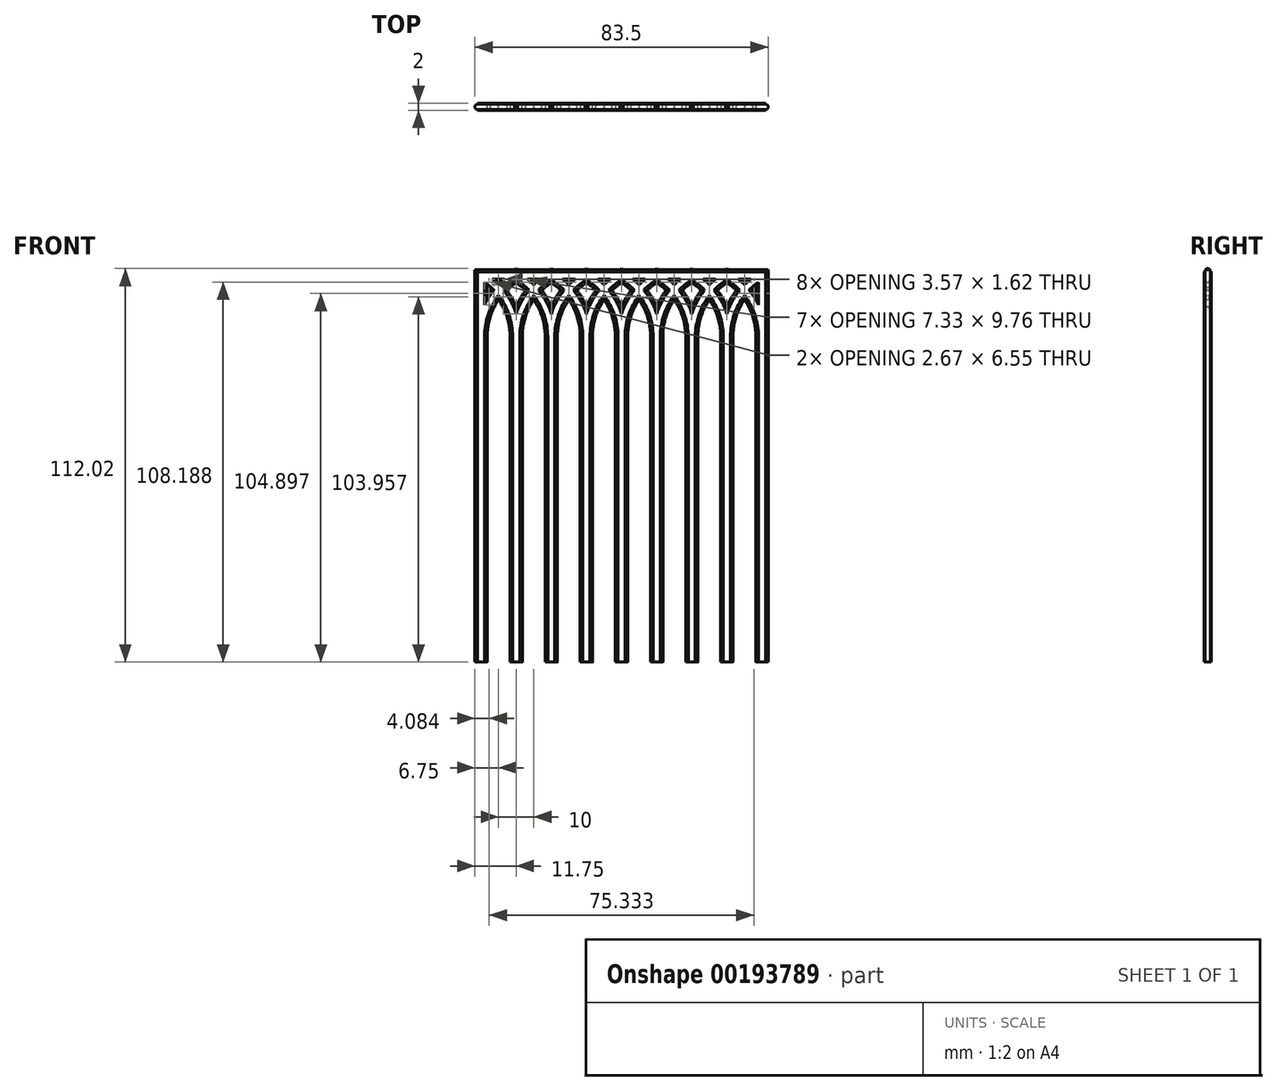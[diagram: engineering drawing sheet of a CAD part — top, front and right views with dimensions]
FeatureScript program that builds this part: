
annotation { "Feature Type Name" : "Feature", "Feature Type Description" : "" }
export const myFeature = defineFeature(function(context is Context, id is Id, definition is map)
    precondition{}
    {
        {
            var Q0;
            Q0=qCreatedBy(makeId("Front.planeOp"),FACE);
            var sketch = newSketch(context, id + "F0", { "sketchPlane" : qUnion([Q0])});
            skLineSegment(sketch, "E0", {"start": v(0, 0) * mm, "end": v(10, 0) * mm, "construction": true});
            skLineSegment(sketch, "E1", {"start": v(10, 0) * mm, "end": v(20, 0) * mm, "construction": true});
            skLineSegment(sketch, "E2", {"start": v(20, 0) * mm, "end": v(30, 0) * mm, "construction": true});
            skLineSegment(sketch, "E3", {"start": v(30, 0) * mm, "end": v(40, 0) * mm, "construction": true});
            skLineSegment(sketch, "E4", {"start": v(0, 0) * mm, "end": v(-10, 0) * mm, "construction": true});
            skLineSegment(sketch, "E5", {"start": v(-10, 0) * mm, "end": v(-20, 0) * mm, "construction": true});
            skLineSegment(sketch, "E6", {"start": v(-20, 0) * mm, "end": v(-30, 0) * mm, "construction": true});
            skLineSegment(sketch, "E7", {"start": v(-30, 0) * mm, "end": v(-40, 0) * mm, "construction": true});
            skLineSegment(sketch, "E8", {"start": v(-40, 0) * mm, "end": v(-40, 92.68) * mm});
            skLineSegment(sketch, "E9", {"start": v(-40, 110) * mm, "end": v(40, 110) * mm});
            skLineSegment(sketch, "E10", {"start": v(40, 110) * mm, "end": v(40, 92.68) * mm});
            skLineSegment(sketch, "E11", {"start": v(-20, 0) * mm, "end": v(-20, 110) * mm, "construction": true});
            skLineSegment(sketch, "E12", {"start": v(0, 0) * mm, "end": v(0, 110) * mm, "construction": true});
            skLineSegment(sketch, "E13", {"start": v(20, 0) * mm, "end": v(20, 110) * mm, "construction": true});
            skLineSegment(sketch, "E14", {"start": v(30, 0) * mm, "end": v(30, 110) * mm, "construction": true});
            skLineSegment(sketch, "E15", {"start": v(10, 0) * mm, "end": v(10, 110) * mm, "construction": true});
            skLineSegment(sketch, "E16", {"start": v(-10, 0) * mm, "end": v(-10, 110) * mm, "construction": true});
            skLineSegment(sketch, "E17", {"start": v(-30, 0) * mm, "end": v(-30, 110) * mm, "construction": true});
            skCircle(sketch, "E18", {"center": v(-30, 110) * mm, "radius": 20 * mm, "construction": true});
            skLineSegment(sketch, "E19", {"start": v(-40, 92.68) * mm, "end": v(-30, 92.68) * mm, "construction": true});
            skLineSegment(sketch, "E20", {"start": v(-30, 92.68) * mm, "end": v(-20, 92.68) * mm, "construction": true});
            skLineSegment(sketch, "E21", {"start": v(-20, 92.68) * mm, "end": v(-10, 92.68) * mm, "construction": true});
            skLineSegment(sketch, "E22", {"start": v(0, 92.68) * mm, "end": v(-10, 92.68) * mm, "construction": true});
            skLineSegment(sketch, "E23", {"start": v(0, 92.68) * mm, "end": v(10, 92.68) * mm, "construction": true});
            skLineSegment(sketch, "E24", {"start": v(10, 92.68) * mm, "end": v(20, 92.68) * mm, "construction": true});
            skLineSegment(sketch, "E25", {"start": v(30, 92.68) * mm, "end": v(20, 92.68) * mm, "construction": true});
            skLineSegment(sketch, "E26", {"start": v(30, 92.68) * mm, "end": v(40, 92.68) * mm, "construction": true});
            skArc(sketch, "E27", {"start": v(-40, 92.68) * mm, "mid": v(-37.32, 102.68) * mm, "end": v(-30, 110) * mm});
            skArc(sketch, "E28", {"start": v(-20, 110) * mm, "mid": v(-27.32, 102.68) * mm, "end": v(-30, 92.68) * mm});
            skArc(sketch, "E29", {"start": v(-10, 110) * mm, "mid": v(-17.32, 102.68) * mm, "end": v(-20, 92.68) * mm});
            skArc(sketch, "E30", {"start": v(-10, 92.68) * mm, "mid": v(-7.32, 102.68) * mm, "end": v(0, 110) * mm});
            skArc(sketch, "E31", {"start": v(10, 110) * mm, "mid": v(2.68, 102.68) * mm, "end": v(0, 92.68) * mm});
            skArc(sketch, "E32", {"start": v(20, 110) * mm, "mid": v(12.68, 102.68) * mm, "end": v(10, 92.68) * mm});
            skArc(sketch, "E33", {"start": v(20, 92.68) * mm, "mid": v(22.68, 102.68) * mm, "end": v(30, 110) * mm});
            skLineSegment(sketch, "E34", {"start": v(40, 92.68) * mm, "end": v(50, 92.68) * mm, "construction": true});
            skLineSegment(sketch, "E35", {"start": v(-40, 92.68) * mm, "end": v(-50, 92.68) * mm, "construction": true});
            skArc(sketch, "E36", {"start": v(-40, 110) * mm, "mid": v(-32.68, 102.68) * mm, "end": v(-30, 92.68) * mm});
            skArc(sketch, "E37", {"start": v(-20, 110) * mm, "mid": v(-12.68, 102.68) * mm, "end": v(-10, 92.68) * mm});
            skArc(sketch, "E38", {"start": v(-30, 110) * mm, "mid": v(-22.68, 102.68) * mm, "end": v(-20, 92.68) * mm});
            skArc(sketch, "E39", {"start": v(0, 110) * mm, "mid": v(7.32, 102.68) * mm, "end": v(10, 92.68) * mm});
            skArc(sketch, "E40", {"start": v(10, 110) * mm, "mid": v(17.32, 102.68) * mm, "end": v(20, 92.68) * mm});
            skArc(sketch, "E41", {"start": v(20, 110) * mm, "mid": v(27.32, 102.68) * mm, "end": v(30, 92.68) * mm});
            skArc(sketch, "E42", {"start": v(30, 110) * mm, "mid": v(37.32, 102.68) * mm, "end": v(40, 92.68) * mm});
            skArc(sketch, "E43", {"start": v(30, 92.68) * mm, "mid": v(32.68, 102.68) * mm, "end": v(40, 110) * mm});
            skArc(sketch, "E44", {"start": v(-10, 110) * mm, "mid": v(-2.68, 102.68) * mm, "end": v(0, 92.68) * mm});
            skLineSegment(sketch, "E45", {"start": v(-30, 92.68) * mm, "end": v(-30, 0) * mm});
            skLineSegment(sketch, "E46", {"start": v(-20, 92.68) * mm, "end": v(-20, 0) * mm});
            skLineSegment(sketch, "E47", {"start": v(-10, 0) * mm, "end": v(-10, 92.68) * mm});
            skLineSegment(sketch, "E48", {"start": v(0, 92.68) * mm, "end": v(0, 0) * mm});
            skLineSegment(sketch, "E49", {"start": v(10, 92.68) * mm, "end": v(10, 0) * mm});
            skLineSegment(sketch, "E50", {"start": v(20, 0) * mm, "end": v(20, 92.68) * mm});
            skLineSegment(sketch, "E51", {"start": v(30, 92.68) * mm, "end": v(30, 0) * mm});
            skLineSegment(sketch, "E52", {"start": v(-40, 92.68) * mm, "end": v(-40, 110) * mm});
            skLineSegment(sketch, "E53", {"start": v(40, 92.68) * mm, "end": v(40, 0) * mm});
            skSolve(sketch);
        }
        {
            var Q0;
            Q0=qCreatedBy(makeId("Top.planeOp"),FACE);
            var sketch = newSketch(context, id + "F1", { "sketchPlane" : qUnion([Q0])});
            skPoint(sketch, "E54.0", {"position": v(-40, 0) * mm});
            skLineSegment(sketch, "E55.bottom", {"start": v(-39, 1) * mm, "end": v(-41, 1) * mm});
            skLineSegment(sketch, "E55.top", {"start": v(-39, -1) * mm, "end": v(-41, -1) * mm});
            skLineSegment(sketch, "E55.left", {"start": v(-39, 1) * mm, "end": v(-39, -1) * mm});
            skLineSegment(sketch, "E55.right", {"start": v(-41, 1) * mm, "end": v(-41, -1) * mm});
            skCircle(sketch, "E56", {"center": v(-39, 0) * mm, "radius": 0.75 * mm});
            skCircle(sketch, "E57", {"center": v(-41, 0) * mm, "radius": 0.75 * mm});
            skPoint(sketch, "E58.1.0.0", {"position": v(-30, 0) * mm});
            skCircle(sketch, "E58.1.0.1", {"center": v(-31, 0) * mm, "radius": 0.75 * mm});
            skLineSegment(sketch, "E58.1.0.2", {"start": v(-29, -1) * mm, "end": v(-31, -1) * mm});
            skLineSegment(sketch, "E58.1.0.3", {"start": v(-31, 1) * mm, "end": v(-31, -1) * mm});
            skLineSegment(sketch, "E58.1.0.4", {"start": v(-29, 1) * mm, "end": v(-31, 1) * mm});
            skCircle(sketch, "E58.1.0.5", {"center": v(-29, 0) * mm, "radius": 0.75 * mm});
            skLineSegment(sketch, "E58.1.0.6", {"start": v(-29, 1) * mm, "end": v(-29, -1) * mm});
            skPoint(sketch, "E58.2.0.0", {"position": v(-20, 0) * mm});
            skCircle(sketch, "E58.2.0.1", {"center": v(-21, 0) * mm, "radius": 0.75 * mm});
            skLineSegment(sketch, "E58.2.0.2", {"start": v(-19, -1) * mm, "end": v(-21, -1) * mm});
            skLineSegment(sketch, "E58.2.0.3", {"start": v(-21, 1) * mm, "end": v(-21, -1) * mm});
            skLineSegment(sketch, "E58.2.0.4", {"start": v(-19, 1) * mm, "end": v(-21, 1) * mm});
            skCircle(sketch, "E58.2.0.5", {"center": v(-19, 0) * mm, "radius": 0.75 * mm});
            skLineSegment(sketch, "E58.2.0.6", {"start": v(-19, 1) * mm, "end": v(-19, -1) * mm});
            skPoint(sketch, "E58.3.0.0", {"position": v(-10, 0) * mm});
            skCircle(sketch, "E58.3.0.1", {"center": v(-11, 0) * mm, "radius": 0.75 * mm});
            skLineSegment(sketch, "E58.3.0.2", {"start": v(-9, -1) * mm, "end": v(-11, -1) * mm});
            skLineSegment(sketch, "E58.3.0.3", {"start": v(-11, 1) * mm, "end": v(-11, -1) * mm});
            skLineSegment(sketch, "E58.3.0.4", {"start": v(-9, 1) * mm, "end": v(-11, 1) * mm});
            skCircle(sketch, "E58.3.0.5", {"center": v(-9, 0) * mm, "radius": 0.75 * mm});
            skLineSegment(sketch, "E58.3.0.6", {"start": v(-9, 1) * mm, "end": v(-9, -1) * mm});
            skPoint(sketch, "E58.4.0.0", {"position": v(0, 0) * mm});
            skCircle(sketch, "E58.4.0.1", {"center": v(-1, 0) * mm, "radius": 0.75 * mm});
            skLineSegment(sketch, "E58.4.0.2", {"start": v(1, -1) * mm, "end": v(-1, -1) * mm});
            skLineSegment(sketch, "E58.4.0.3", {"start": v(-1, 1) * mm, "end": v(-1, -1) * mm});
            skLineSegment(sketch, "E58.4.0.4", {"start": v(1, 1) * mm, "end": v(-1, 1) * mm});
            skCircle(sketch, "E58.4.0.5", {"center": v(1, 0) * mm, "radius": 0.75 * mm});
            skLineSegment(sketch, "E58.4.0.6", {"start": v(1, 1) * mm, "end": v(1, -1) * mm});
            skPoint(sketch, "E58.5.0.0", {"position": v(10, 0) * mm});
            skCircle(sketch, "E58.5.0.1", {"center": v(9, 0) * mm, "radius": 0.75 * mm});
            skLineSegment(sketch, "E58.5.0.2", {"start": v(11, -1) * mm, "end": v(9, -1) * mm});
            skLineSegment(sketch, "E58.5.0.3", {"start": v(9, 1) * mm, "end": v(9, -1) * mm});
            skLineSegment(sketch, "E58.5.0.4", {"start": v(11, 1) * mm, "end": v(9, 1) * mm});
            skCircle(sketch, "E58.5.0.5", {"center": v(11, 0) * mm, "radius": 0.75 * mm});
            skLineSegment(sketch, "E58.5.0.6", {"start": v(11, 1) * mm, "end": v(11, -1) * mm});
            skPoint(sketch, "E58.6.0.0", {"position": v(20, 0) * mm});
            skCircle(sketch, "E58.6.0.1", {"center": v(19, 0) * mm, "radius": 0.75 * mm});
            skLineSegment(sketch, "E58.6.0.2", {"start": v(21, -1) * mm, "end": v(19, -1) * mm});
            skLineSegment(sketch, "E58.6.0.3", {"start": v(19, 1) * mm, "end": v(19, -1) * mm});
            skLineSegment(sketch, "E58.6.0.4", {"start": v(21, 1) * mm, "end": v(19, 1) * mm});
            skCircle(sketch, "E58.6.0.5", {"center": v(21, 0) * mm, "radius": 0.75 * mm});
            skLineSegment(sketch, "E58.6.0.6", {"start": v(21, 1) * mm, "end": v(21, -1) * mm});
            skPoint(sketch, "E58.7.0.0", {"position": v(30, 0) * mm});
            skCircle(sketch, "E58.7.0.1", {"center": v(29, 0) * mm, "radius": 0.75 * mm});
            skLineSegment(sketch, "E58.7.0.2", {"start": v(31, -1) * mm, "end": v(29, -1) * mm});
            skLineSegment(sketch, "E58.7.0.3", {"start": v(29, 1) * mm, "end": v(29, -1) * mm});
            skLineSegment(sketch, "E58.7.0.4", {"start": v(31, 1) * mm, "end": v(29, 1) * mm});
            skCircle(sketch, "E58.7.0.5", {"center": v(31, 0) * mm, "radius": 0.75 * mm});
            skLineSegment(sketch, "E58.7.0.6", {"start": v(31, 1) * mm, "end": v(31, -1) * mm});
            skPoint(sketch, "E58.8.0.0", {"position": v(40, 0) * mm});
            skCircle(sketch, "E58.8.0.1", {"center": v(39, 0) * mm, "radius": 0.75 * mm});
            skLineSegment(sketch, "E58.8.0.2", {"start": v(41, -1) * mm, "end": v(39, -1) * mm});
            skLineSegment(sketch, "E58.8.0.3", {"start": v(39, 1) * mm, "end": v(39, -1) * mm});
            skLineSegment(sketch, "E58.8.0.4", {"start": v(41, 1) * mm, "end": v(39, 1) * mm});
            skCircle(sketch, "E58.8.0.5", {"center": v(41, 0) * mm, "radius": 0.75 * mm});
            skLineSegment(sketch, "E58.8.0.6", {"start": v(41, 1) * mm, "end": v(41, -1) * mm});
            skLineSegment(sketch, "E58.direction1", {"start": v(-40, 0) * mm, "end": v(-30, 0) * mm, "construction": true});
            skSolve(sketch);
        }
        {
            var Q0;
            {var subQ0=sQuery(id+"F1.wireOp",EDGE,"E57");var subQ1=sQuery(id+"F1.wireOp",EDGE,"E55.right");var subQ2=makeQuery(id+"F1.imprint","INTERSECT",VERTEX,{"disambiguationData":[OD(0.0)],"derivedFrom":[subQ1,subQ0]});Q0=makeQuery(id+"F1.imprint","IMPRINT",FACE,{"disambiguationData":[TD([[makeQuery(id+"F1.imprint","IMPRINT",EDGE,{"disambiguationData":[TD([[subQ2,-1.0]])],"derivedFrom":subQ1}),-1.0]])]});}
            var Q1;
            {var subQ0=sQuery(id+"F1.wireOp",EDGE,"E57");var subQ1=sQuery(id+"F1.wireOp",EDGE,"E55.right");var subQ2=makeQuery(id+"F1.imprint","INTERSECT",VERTEX,{"disambiguationData":[OD(0.0)],"derivedFrom":[subQ1,subQ0]});Q1=makeQuery(id+"F1.imprint","IMPRINT",FACE,{"disambiguationData":[TD([[makeQuery(id+"F1.imprint","IMPRINT",EDGE,{"disambiguationData":[TD([[subQ2,-1.0]])],"derivedFrom":subQ1}),1.0]])]});}
            var Q2;
            {var subQ4=sQuery(id+"F1.wireOp",EDGE,"E55.bottom");Q2=makeQuery(id+"F1.imprint","IMPRINT",FACE,{"disambiguationData":[TD([[makeQuery(id+"F1.imprint","IMPRINT",EDGE,{"derivedFrom":subQ4}),1.0]])]});}
            var Q3;
            {var subQ0=sQuery(id+"F1.wireOp",EDGE,"E56");var subQ1=sQuery(id+"F1.wireOp",EDGE,"E55.left");var subQ2=makeQuery(id+"F1.imprint","INTERSECT",VERTEX,{"disambiguationData":[OD(0.0)],"derivedFrom":[subQ1,subQ0]});Q3=makeQuery(id+"F1.imprint","IMPRINT",FACE,{"disambiguationData":[TD([[makeQuery(id+"F1.imprint","IMPRINT",EDGE,{"disambiguationData":[TD([[subQ2,-1.0]])],"derivedFrom":subQ1}),-1.0]])]});}
            var Q4;
            {var subQ0=sQuery(id+"F1.wireOp",EDGE,"E56");var subQ1=sQuery(id+"F1.wireOp",EDGE,"E55.left");var subQ2=makeQuery(id+"F1.imprint","INTERSECT",VERTEX,{"disambiguationData":[OD(0.0)],"derivedFrom":[subQ1,subQ0]});Q4=makeQuery(id+"F1.imprint","IMPRINT",FACE,{"disambiguationData":[TD([[makeQuery(id+"F1.imprint","IMPRINT",EDGE,{"disambiguationData":[TD([[subQ2,-1.0]])],"derivedFrom":subQ1}),1.0]])]});}
            var Q5;
            Q5=sQuery(id+"F0.wireOp",EDGE,"E8");
            var Q6;
            Q6=sQuery(id+"F0.wireOp",EDGE,"E9");
            var Q7;
            Q7=sQuery(id+"F0.wireOp",EDGE,"E52");
            var Q8;
            Q8=sQuery(id+"F0.wireOp",EDGE,"E10");
            sweep(context, id + "F2", {"profiles" : qUnion([Q0, Q1, Q2, Q3, Q4]), "path" : qUnion([Q5, Q6, Q7, Q8])});
        }
        {
            var Q0;
            Q0=makeQuery(id+"F2.opSweep","CAP_FACE",FACE,{"disambiguationData":[OSD([sQuery(id+"F0.wireOp",VERTEX,"E8.start"),sQuery(id+"F1.wireOp",EDGE,"E55.bottom"),sQuery(id+"F1.wireOp",EDGE,"E55.top"),sQuery(id+"F1.wireOp",EDGE,"E55.left"),sQuery(id+"F1.wireOp",EDGE,"E55.right"),sQuery(id+"F1.wireOp",EDGE,"E56"),sQuery(id+"F1.wireOp",EDGE,"E57")])],"isStart":true});
            var Q1;
            Q1=sQuery(id+"F0.wireOp",EDGE,"E27");
            var Q2;
            Q2=sQuery(id+"F0.wireOp",EDGE,"E8");
            var Q3;
            Q3=sQuery(id+"F0.wireOp",EDGE,"E38");
            sweep(context, id + "F3", {"operationType" : NewBodyOperationType.ADD, "profiles" : qUnion([Q0]), "path" : qUnion([Q1, Q2, Q3])});
        }
        {
            var Q0;
            {var subQ1=sQuery(id+"F1.wireOp",EDGE,"E58.1.0.2");Q0=makeQuery(id+"F1.imprint","IMPRINT",FACE,{"disambiguationData":[TD([[makeQuery(id+"F1.imprint","IMPRINT",EDGE,{"derivedFrom":subQ1}),-1.0]])]});}
            var Q1;
            {var subQ0=sQuery(id+"F1.wireOp",EDGE,"E58.1.0.3");var subQ1=sQuery(id+"F1.wireOp",EDGE,"E58.1.0.1");var subQ2=makeQuery(id+"F1.imprint","INTERSECT",VERTEX,{"disambiguationData":[OD(0.0)],"derivedFrom":[subQ1,subQ0]});Q1=makeQuery(id+"F1.imprint","IMPRINT",FACE,{"disambiguationData":[TD([[makeQuery(id+"F1.imprint","IMPRINT",EDGE,{"disambiguationData":[TD([[subQ2,1.0]])],"derivedFrom":subQ1}),1.0]])]});}
            var Q2;
            {var subQ0=sQuery(id+"F1.wireOp",EDGE,"E58.1.0.3");var subQ1=sQuery(id+"F1.wireOp",EDGE,"E58.1.0.1");var subQ2=makeQuery(id+"F1.imprint","INTERSECT",VERTEX,{"disambiguationData":[OD(0.0)],"derivedFrom":[subQ1,subQ0]});Q2=makeQuery(id+"F1.imprint","IMPRINT",FACE,{"disambiguationData":[TD([[makeQuery(id+"F1.imprint","IMPRINT",EDGE,{"disambiguationData":[TD([[subQ2,-1.0]])],"derivedFrom":subQ1}),1.0]])]});}
            var Q3;
            {var subQ0=sQuery(id+"F1.wireOp",EDGE,"E58.1.0.6");var subQ1=sQuery(id+"F1.wireOp",EDGE,"E58.1.0.5");var subQ2=makeQuery(id+"F1.imprint","INTERSECT",VERTEX,{"disambiguationData":[OD(0.0)],"derivedFrom":[subQ1,subQ0]});Q3=makeQuery(id+"F1.imprint","IMPRINT",FACE,{"disambiguationData":[TD([[makeQuery(id+"F1.imprint","IMPRINT",EDGE,{"disambiguationData":[TD([[subQ2,-1.0]])],"derivedFrom":subQ1}),1.0]])]});}
            var Q4;
            {var subQ0=sQuery(id+"F1.wireOp",EDGE,"E58.1.0.6");var subQ1=sQuery(id+"F1.wireOp",EDGE,"E58.1.0.5");var subQ2=makeQuery(id+"F1.imprint","INTERSECT",VERTEX,{"disambiguationData":[OD(0.0)],"derivedFrom":[subQ1,subQ0]});Q4=makeQuery(id+"F1.imprint","IMPRINT",FACE,{"disambiguationData":[TD([[makeQuery(id+"F1.imprint","IMPRINT",EDGE,{"disambiguationData":[TD([[subQ2,1.0]])],"derivedFrom":subQ1}),1.0]])]});}
            var Q5;
            Q5=sQuery(id+"F0.wireOp",EDGE,"E45");
            var Q6;
            Q6=sQuery(id+"F0.wireOp",EDGE,"E28");
            var Q7;
            Q7=sQuery(id+"F0.wireOp",EDGE,"E37");
            sweep(context, id + "F4", {"operationType" : NewBodyOperationType.ADD, "profiles" : qUnion([Q0, Q1, Q2, Q3, Q4]), "path" : qUnion([Q5, Q6, Q7])});
        }
        {
            var Q0;
            {var subQ1=sQuery(id+"F1.wireOp",EDGE,"E58.2.0.2");Q0=makeQuery(id+"F1.imprint","IMPRINT",FACE,{"disambiguationData":[TD([[makeQuery(id+"F1.imprint","IMPRINT",EDGE,{"derivedFrom":subQ1}),-1.0]])]});}
            var Q1;
            {var subQ0=sQuery(id+"F1.wireOp",EDGE,"E58.2.0.6");var subQ1=sQuery(id+"F1.wireOp",EDGE,"E58.2.0.5");var subQ2=makeQuery(id+"F1.imprint","INTERSECT",VERTEX,{"disambiguationData":[OD(0.0)],"derivedFrom":[subQ1,subQ0]});Q1=makeQuery(id+"F1.imprint","IMPRINT",FACE,{"disambiguationData":[TD([[makeQuery(id+"F1.imprint","IMPRINT",EDGE,{"disambiguationData":[TD([[subQ2,-1.0]])],"derivedFrom":subQ1}),1.0]])]});}
            var Q2;
            {var subQ0=sQuery(id+"F1.wireOp",EDGE,"E58.2.0.6");var subQ1=sQuery(id+"F1.wireOp",EDGE,"E58.2.0.5");var subQ2=makeQuery(id+"F1.imprint","INTERSECT",VERTEX,{"disambiguationData":[OD(0.0)],"derivedFrom":[subQ1,subQ0]});Q2=makeQuery(id+"F1.imprint","IMPRINT",FACE,{"disambiguationData":[TD([[makeQuery(id+"F1.imprint","IMPRINT",EDGE,{"disambiguationData":[TD([[subQ2,1.0]])],"derivedFrom":subQ1}),1.0]])]});}
            var Q3;
            {var subQ0=sQuery(id+"F1.wireOp",EDGE,"E58.2.0.3");var subQ1=sQuery(id+"F1.wireOp",EDGE,"E58.2.0.1");var subQ2=makeQuery(id+"F1.imprint","INTERSECT",VERTEX,{"disambiguationData":[OD(0.0)],"derivedFrom":[subQ1,subQ0]});Q3=makeQuery(id+"F1.imprint","IMPRINT",FACE,{"disambiguationData":[TD([[makeQuery(id+"F1.imprint","IMPRINT",EDGE,{"disambiguationData":[TD([[subQ2,-1.0]])],"derivedFrom":subQ1}),1.0]])]});}
            var Q4;
            {var subQ0=sQuery(id+"F1.wireOp",EDGE,"E58.2.0.3");var subQ1=sQuery(id+"F1.wireOp",EDGE,"E58.2.0.1");var subQ2=makeQuery(id+"F1.imprint","INTERSECT",VERTEX,{"disambiguationData":[OD(0.0)],"derivedFrom":[subQ1,subQ0]});Q4=makeQuery(id+"F1.imprint","IMPRINT",FACE,{"disambiguationData":[TD([[makeQuery(id+"F1.imprint","IMPRINT",EDGE,{"disambiguationData":[TD([[subQ2,1.0]])],"derivedFrom":subQ1}),1.0]])]});}
            var Q5;
            Q5=sQuery(id+"F0.wireOp",EDGE,"E46");
            var Q6;
            Q6=sQuery(id+"F0.wireOp",EDGE,"E29");
            var Q7;
            Q7=sQuery(id+"F0.wireOp",EDGE,"E44");
            sweep(context, id + "F5", {"operationType" : NewBodyOperationType.ADD, "profiles" : qUnion([Q0, Q1, Q2, Q3, Q4]), "path" : qUnion([Q5, Q6, Q7])});
        }
        {
            var Q0;
            {var subQ0=sQuery(id+"F1.wireOp",EDGE,"E58.3.0.3");var subQ1=sQuery(id+"F1.wireOp",EDGE,"E58.3.0.1");var subQ2=makeQuery(id+"F1.imprint","INTERSECT",VERTEX,{"disambiguationData":[OD(0.0)],"derivedFrom":[subQ1,subQ0]});Q0=makeQuery(id+"F1.imprint","IMPRINT",FACE,{"disambiguationData":[TD([[makeQuery(id+"F1.imprint","IMPRINT",EDGE,{"disambiguationData":[TD([[subQ2,1.0]])],"derivedFrom":subQ1}),1.0]])]});}
            var Q1;
            {var subQ0=sQuery(id+"F1.wireOp",EDGE,"E58.3.0.3");var subQ1=sQuery(id+"F1.wireOp",EDGE,"E58.3.0.1");var subQ2=makeQuery(id+"F1.imprint","INTERSECT",VERTEX,{"disambiguationData":[OD(0.0)],"derivedFrom":[subQ1,subQ0]});Q1=makeQuery(id+"F1.imprint","IMPRINT",FACE,{"disambiguationData":[TD([[makeQuery(id+"F1.imprint","IMPRINT",EDGE,{"disambiguationData":[TD([[subQ2,-1.0]])],"derivedFrom":subQ1}),1.0]])]});}
            var Q2;
            {var subQ0=sQuery(id+"F1.wireOp",EDGE,"E58.3.0.6");var subQ1=sQuery(id+"F1.wireOp",EDGE,"E58.3.0.5");var subQ2=makeQuery(id+"F1.imprint","INTERSECT",VERTEX,{"disambiguationData":[OD(0.0)],"derivedFrom":[subQ1,subQ0]});Q2=makeQuery(id+"F1.imprint","IMPRINT",FACE,{"disambiguationData":[TD([[makeQuery(id+"F1.imprint","IMPRINT",EDGE,{"disambiguationData":[TD([[subQ2,1.0]])],"derivedFrom":subQ1}),1.0]])]});}
            var Q3;
            {var subQ1=sQuery(id+"F1.wireOp",EDGE,"E58.3.0.2");Q3=makeQuery(id+"F1.imprint","IMPRINT",FACE,{"disambiguationData":[TD([[makeQuery(id+"F1.imprint","IMPRINT",EDGE,{"derivedFrom":subQ1}),-1.0]])]});}
            var Q4;
            {var subQ0=sQuery(id+"F1.wireOp",EDGE,"E58.3.0.6");var subQ1=sQuery(id+"F1.wireOp",EDGE,"E58.3.0.5");var subQ2=makeQuery(id+"F1.imprint","INTERSECT",VERTEX,{"disambiguationData":[OD(0.0)],"derivedFrom":[subQ1,subQ0]});Q4=makeQuery(id+"F1.imprint","IMPRINT",FACE,{"disambiguationData":[TD([[makeQuery(id+"F1.imprint","IMPRINT",EDGE,{"disambiguationData":[TD([[subQ2,-1.0]])],"derivedFrom":subQ1}),1.0]])]});}
            var Q5;
            Q5=sQuery(id+"F0.wireOp",EDGE,"E47");
            var Q6;
            Q6=sQuery(id+"F0.wireOp",EDGE,"E30");
            var Q7;
            Q7=sQuery(id+"F0.wireOp",EDGE,"E39");
            sweep(context, id + "F6", {"operationType" : NewBodyOperationType.ADD, "profiles" : qUnion([Q0, Q1, Q2, Q3, Q4]), "path" : qUnion([Q5, Q6, Q7])});
        }
        {
            var Q0;
            {var subQ0=sQuery(id+"F1.wireOp",EDGE,"E58.4.0.6");var subQ1=sQuery(id+"F1.wireOp",EDGE,"E58.4.0.5");var subQ2=makeQuery(id+"F1.imprint","INTERSECT",VERTEX,{"disambiguationData":[OD(0.0)],"derivedFrom":[subQ1,subQ0]});Q0=makeQuery(id+"F1.imprint","IMPRINT",FACE,{"disambiguationData":[TD([[makeQuery(id+"F1.imprint","IMPRINT",EDGE,{"disambiguationData":[TD([[subQ2,-1.0]])],"derivedFrom":subQ1}),1.0]])]});}
            var Q1;
            {var subQ1=sQuery(id+"F1.wireOp",EDGE,"E58.4.0.2");Q1=makeQuery(id+"F1.imprint","IMPRINT",FACE,{"disambiguationData":[TD([[makeQuery(id+"F1.imprint","IMPRINT",EDGE,{"derivedFrom":subQ1}),-1.0]])]});}
            var Q2;
            {var subQ0=sQuery(id+"F1.wireOp",EDGE,"E58.4.0.3");var subQ1=sQuery(id+"F1.wireOp",EDGE,"E58.4.0.1");var subQ2=makeQuery(id+"F1.imprint","INTERSECT",VERTEX,{"disambiguationData":[OD(0.0)],"derivedFrom":[subQ1,subQ0]});Q2=makeQuery(id+"F1.imprint","IMPRINT",FACE,{"disambiguationData":[TD([[makeQuery(id+"F1.imprint","IMPRINT",EDGE,{"disambiguationData":[TD([[subQ2,-1.0]])],"derivedFrom":subQ1}),1.0]])]});}
            var Q3;
            {var subQ0=sQuery(id+"F1.wireOp",EDGE,"E58.4.0.6");var subQ1=sQuery(id+"F1.wireOp",EDGE,"E58.4.0.5");var subQ2=makeQuery(id+"F1.imprint","INTERSECT",VERTEX,{"disambiguationData":[OD(0.0)],"derivedFrom":[subQ1,subQ0]});Q3=makeQuery(id+"F1.imprint","IMPRINT",FACE,{"disambiguationData":[TD([[makeQuery(id+"F1.imprint","IMPRINT",EDGE,{"disambiguationData":[TD([[subQ2,1.0]])],"derivedFrom":subQ1}),1.0]])]});}
            var Q4;
            {var subQ0=sQuery(id+"F1.wireOp",EDGE,"E58.4.0.3");var subQ1=sQuery(id+"F1.wireOp",EDGE,"E58.4.0.1");var subQ2=makeQuery(id+"F1.imprint","INTERSECT",VERTEX,{"disambiguationData":[OD(0.0)],"derivedFrom":[subQ1,subQ0]});Q4=makeQuery(id+"F1.imprint","IMPRINT",FACE,{"disambiguationData":[TD([[makeQuery(id+"F1.imprint","IMPRINT",EDGE,{"disambiguationData":[TD([[subQ2,1.0]])],"derivedFrom":subQ1}),1.0]])]});}
            var Q5;
            Q5=sQuery(id+"F0.wireOp",EDGE,"E48");
            var Q6;
            Q6=sQuery(id+"F0.wireOp",EDGE,"E31");
            var Q7;
            Q7=sQuery(id+"F0.wireOp",EDGE,"E40");
            sweep(context, id + "F7", {"operationType" : NewBodyOperationType.ADD, "profiles" : qUnion([Q0, Q1, Q2, Q3, Q4]), "path" : qUnion([Q5, Q6, Q7])});
        }
        {
            var Q0;
            {var subQ0=sQuery(id+"F1.wireOp",EDGE,"E58.5.0.3");var subQ1=sQuery(id+"F1.wireOp",EDGE,"E58.5.0.1");var subQ2=makeQuery(id+"F1.imprint","INTERSECT",VERTEX,{"disambiguationData":[OD(0.0)],"derivedFrom":[subQ1,subQ0]});Q0=makeQuery(id+"F1.imprint","IMPRINT",FACE,{"disambiguationData":[TD([[makeQuery(id+"F1.imprint","IMPRINT",EDGE,{"disambiguationData":[TD([[subQ2,-1.0]])],"derivedFrom":subQ1}),1.0]])]});}
            var Q1;
            {var subQ0=sQuery(id+"F1.wireOp",EDGE,"E58.5.0.6");var subQ1=sQuery(id+"F1.wireOp",EDGE,"E58.5.0.5");var subQ2=makeQuery(id+"F1.imprint","INTERSECT",VERTEX,{"disambiguationData":[OD(0.0)],"derivedFrom":[subQ1,subQ0]});Q1=makeQuery(id+"F1.imprint","IMPRINT",FACE,{"disambiguationData":[TD([[makeQuery(id+"F1.imprint","IMPRINT",EDGE,{"disambiguationData":[TD([[subQ2,1.0]])],"derivedFrom":subQ1}),1.0]])]});}
            var Q2;
            {var subQ0=sQuery(id+"F1.wireOp",EDGE,"E58.5.0.3");var subQ1=sQuery(id+"F1.wireOp",EDGE,"E58.5.0.1");var subQ2=makeQuery(id+"F1.imprint","INTERSECT",VERTEX,{"disambiguationData":[OD(0.0)],"derivedFrom":[subQ1,subQ0]});Q2=makeQuery(id+"F1.imprint","IMPRINT",FACE,{"disambiguationData":[TD([[makeQuery(id+"F1.imprint","IMPRINT",EDGE,{"disambiguationData":[TD([[subQ2,1.0]])],"derivedFrom":subQ1}),1.0]])]});}
            var Q3;
            {var subQ1=sQuery(id+"F1.wireOp",EDGE,"E58.5.0.2");Q3=makeQuery(id+"F1.imprint","IMPRINT",FACE,{"disambiguationData":[TD([[makeQuery(id+"F1.imprint","IMPRINT",EDGE,{"derivedFrom":subQ1}),-1.0]])]});}
            var Q4;
            {var subQ0=sQuery(id+"F1.wireOp",EDGE,"E58.5.0.6");var subQ1=sQuery(id+"F1.wireOp",EDGE,"E58.5.0.5");var subQ2=makeQuery(id+"F1.imprint","INTERSECT",VERTEX,{"disambiguationData":[OD(0.0)],"derivedFrom":[subQ1,subQ0]});Q4=makeQuery(id+"F1.imprint","IMPRINT",FACE,{"disambiguationData":[TD([[makeQuery(id+"F1.imprint","IMPRINT",EDGE,{"disambiguationData":[TD([[subQ2,-1.0]])],"derivedFrom":subQ1}),1.0]])]});}
            var Q5;
            Q5=sQuery(id+"F0.wireOp",EDGE,"E49");
            var Q6;
            Q6=sQuery(id+"F0.wireOp",EDGE,"E32");
            var Q7;
            Q7=sQuery(id+"F0.wireOp",EDGE,"E41");
            sweep(context, id + "F8", {"operationType" : NewBodyOperationType.ADD, "profiles" : qUnion([Q0, Q1, Q2, Q3, Q4]), "path" : qUnion([Q5, Q6, Q7])});
        }
        {
            var Q0;
            {var subQ0=sQuery(id+"F1.wireOp",EDGE,"E58.6.0.3");var subQ1=sQuery(id+"F1.wireOp",EDGE,"E58.6.0.1");var subQ2=makeQuery(id+"F1.imprint","INTERSECT",VERTEX,{"disambiguationData":[OD(0.0)],"derivedFrom":[subQ1,subQ0]});Q0=makeQuery(id+"F1.imprint","IMPRINT",FACE,{"disambiguationData":[TD([[makeQuery(id+"F1.imprint","IMPRINT",EDGE,{"disambiguationData":[TD([[subQ2,-1.0]])],"derivedFrom":subQ1}),1.0]])]});}
            var Q1;
            {var subQ0=sQuery(id+"F1.wireOp",EDGE,"E58.6.0.6");var subQ1=sQuery(id+"F1.wireOp",EDGE,"E58.6.0.5");var subQ2=makeQuery(id+"F1.imprint","INTERSECT",VERTEX,{"disambiguationData":[OD(0.0)],"derivedFrom":[subQ1,subQ0]});Q1=makeQuery(id+"F1.imprint","IMPRINT",FACE,{"disambiguationData":[TD([[makeQuery(id+"F1.imprint","IMPRINT",EDGE,{"disambiguationData":[TD([[subQ2,1.0]])],"derivedFrom":subQ1}),1.0]])]});}
            var Q2;
            {var subQ0=sQuery(id+"F1.wireOp",EDGE,"E58.6.0.6");var subQ1=sQuery(id+"F1.wireOp",EDGE,"E58.6.0.5");var subQ2=makeQuery(id+"F1.imprint","INTERSECT",VERTEX,{"disambiguationData":[OD(0.0)],"derivedFrom":[subQ1,subQ0]});Q2=makeQuery(id+"F1.imprint","IMPRINT",FACE,{"disambiguationData":[TD([[makeQuery(id+"F1.imprint","IMPRINT",EDGE,{"disambiguationData":[TD([[subQ2,-1.0]])],"derivedFrom":subQ1}),1.0]])]});}
            var Q3;
            {var subQ0=sQuery(id+"F1.wireOp",EDGE,"E58.6.0.3");var subQ1=sQuery(id+"F1.wireOp",EDGE,"E58.6.0.1");var subQ2=makeQuery(id+"F1.imprint","INTERSECT",VERTEX,{"disambiguationData":[OD(0.0)],"derivedFrom":[subQ1,subQ0]});Q3=makeQuery(id+"F1.imprint","IMPRINT",FACE,{"disambiguationData":[TD([[makeQuery(id+"F1.imprint","IMPRINT",EDGE,{"disambiguationData":[TD([[subQ2,1.0]])],"derivedFrom":subQ1}),1.0]])]});}
            var Q4;
            {var subQ1=sQuery(id+"F1.wireOp",EDGE,"E58.6.0.2");Q4=makeQuery(id+"F1.imprint","IMPRINT",FACE,{"disambiguationData":[TD([[makeQuery(id+"F1.imprint","IMPRINT",EDGE,{"derivedFrom":subQ1}),-1.0]])]});}
            var Q5;
            Q5=sQuery(id+"F0.wireOp",EDGE,"E50");
            var Q6;
            Q6=sQuery(id+"F0.wireOp",EDGE,"E33");
            var Q7;
            Q7=sQuery(id+"F0.wireOp",EDGE,"E53");
            var Q8;
            Q8=sQuery(id+"F0.wireOp",EDGE,"E42");
            sweep(context, id + "F9", {"operationType" : NewBodyOperationType.ADD, "profiles" : qUnion([Q0, Q1, Q2, Q3, Q4]), "path" : qUnion([Q5, Q6, Q7, Q8])});
        }
        {
            var Q0;
            {var subQ0=sQuery(id+"F1.wireOp",EDGE,"E58.7.0.3");var subQ1=sQuery(id+"F1.wireOp",EDGE,"E58.7.0.1");var subQ2=makeQuery(id+"F1.imprint","INTERSECT",VERTEX,{"disambiguationData":[OD(0.0)],"derivedFrom":[subQ1,subQ0]});Q0=makeQuery(id+"F1.imprint","IMPRINT",FACE,{"disambiguationData":[TD([[makeQuery(id+"F1.imprint","IMPRINT",EDGE,{"disambiguationData":[TD([[subQ2,-1.0]])],"derivedFrom":subQ1}),1.0]])]});}
            var Q1;
            {var subQ0=sQuery(id+"F1.wireOp",EDGE,"E58.7.0.6");var subQ1=sQuery(id+"F1.wireOp",EDGE,"E58.7.0.5");var subQ2=makeQuery(id+"F1.imprint","INTERSECT",VERTEX,{"disambiguationData":[OD(0.0)],"derivedFrom":[subQ1,subQ0]});Q1=makeQuery(id+"F1.imprint","IMPRINT",FACE,{"disambiguationData":[TD([[makeQuery(id+"F1.imprint","IMPRINT",EDGE,{"disambiguationData":[TD([[subQ2,1.0]])],"derivedFrom":subQ1}),1.0]])]});}
            var Q2;
            {var subQ1=sQuery(id+"F1.wireOp",EDGE,"E58.7.0.2");Q2=makeQuery(id+"F1.imprint","IMPRINT",FACE,{"disambiguationData":[TD([[makeQuery(id+"F1.imprint","IMPRINT",EDGE,{"derivedFrom":subQ1}),-1.0]])]});}
            var Q3;
            {var subQ0=sQuery(id+"F1.wireOp",EDGE,"E58.7.0.6");var subQ1=sQuery(id+"F1.wireOp",EDGE,"E58.7.0.5");var subQ2=makeQuery(id+"F1.imprint","INTERSECT",VERTEX,{"disambiguationData":[OD(0.0)],"derivedFrom":[subQ1,subQ0]});Q3=makeQuery(id+"F1.imprint","IMPRINT",FACE,{"disambiguationData":[TD([[makeQuery(id+"F1.imprint","IMPRINT",EDGE,{"disambiguationData":[TD([[subQ2,-1.0]])],"derivedFrom":subQ1}),1.0]])]});}
            var Q4;
            {var subQ0=sQuery(id+"F1.wireOp",EDGE,"E58.7.0.3");var subQ1=sQuery(id+"F1.wireOp",EDGE,"E58.7.0.1");var subQ2=makeQuery(id+"F1.imprint","INTERSECT",VERTEX,{"disambiguationData":[OD(0.0)],"derivedFrom":[subQ1,subQ0]});Q4=makeQuery(id+"F1.imprint","IMPRINT",FACE,{"disambiguationData":[TD([[makeQuery(id+"F1.imprint","IMPRINT",EDGE,{"disambiguationData":[TD([[subQ2,1.0]])],"derivedFrom":subQ1}),1.0]])]});}
            var Q5;
            Q5=sQuery(id+"F0.wireOp",EDGE,"E51");
            var Q6;
            Q6=sQuery(id+"F0.wireOp",EDGE,"E43");
            sweep(context, id + "F10", {"operationType" : NewBodyOperationType.ADD, "profiles" : qUnion([Q0, Q1, Q2, Q3, Q4]), "path" : qUnion([Q5, Q6])});
        }
        {
            var Q0;
            Q0=makeQuery(id+"F4.opSweep","CAP_FACE",FACE,{"disambiguationData":[OSD([sQuery(id+"F0.wireOp",VERTEX,"E45.end"),sQuery(id+"F1.wireOp",EDGE,"E58.1.0.1"),sQuery(id+"F1.wireOp",EDGE,"E58.1.0.2"),sQuery(id+"F1.wireOp",EDGE,"E58.1.0.3"),sQuery(id+"F1.wireOp",EDGE,"E58.1.0.4"),sQuery(id+"F1.wireOp",EDGE,"E58.1.0.5"),sQuery(id+"F1.wireOp",EDGE,"E58.1.0.6")])],"isStart":true});
            var Q1;
            Q1=sQuery(id+"F0.wireOp",EDGE,"E45");
            var Q2;
            Q2=sQuery(id+"F0.wireOp",EDGE,"E36");
            sweep(context, id + "F11", {"operationType" : NewBodyOperationType.ADD, "profiles" : qUnion([Q0]), "path" : qUnion([Q1, Q2])});
        }
    });
